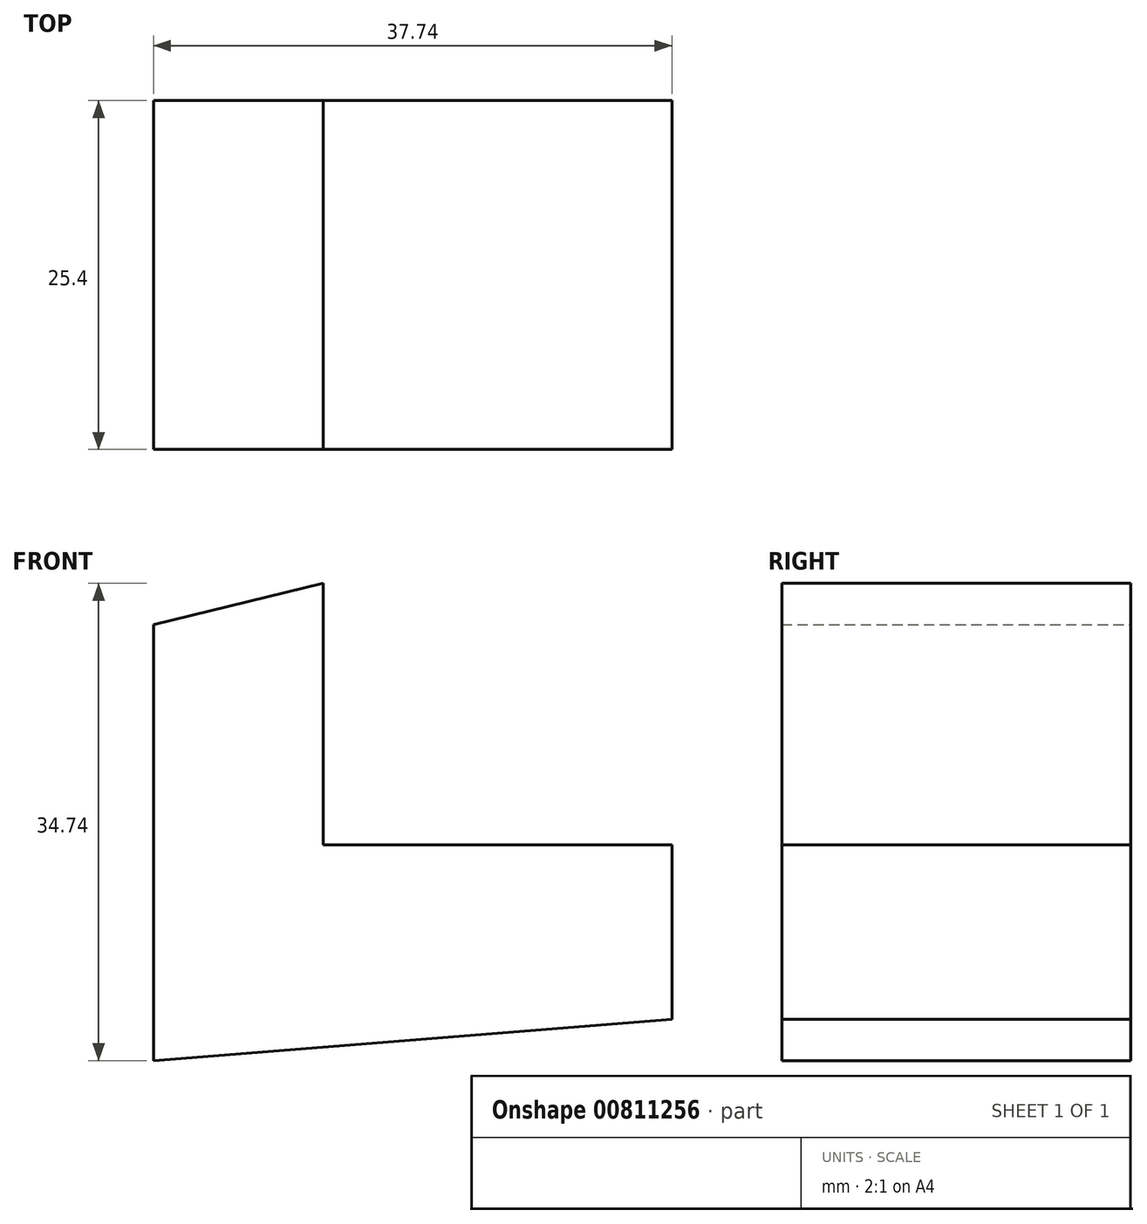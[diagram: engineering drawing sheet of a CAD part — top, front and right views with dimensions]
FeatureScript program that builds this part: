
annotation { "Feature Type Name" : "Feature", "Feature Type Description" : "" }
export const myFeature = defineFeature(function(context is Context, id is Id, definition is map)
    precondition{}
    {
        {
            var Q0;
            Q0=qCreatedBy(makeId("Front.planeOp"),FACE);
            var sketch = newSketch(context, id + "F0", { "sketchPlane" : qUnion([Q0])});
            skLineSegment(sketch, "E0", {"start": v(0, 0) * mm, "end": v(0, 31.75) * mm});
            skLineSegment(sketch, "E1", {"start": v(0, 31.75) * mm, "end": v(12.34, 34.74) * mm});
            skLineSegment(sketch, "E2", {"start": v(12.34, 34.74) * mm, "end": v(12.34, 15.7) * mm});
            skLineSegment(sketch, "E3", {"start": v(12.34, 15.7) * mm, "end": v(37.74, 15.7) * mm});
            skLineSegment(sketch, "E4", {"start": v(37.74, 15.7) * mm, "end": v(37.74, 3) * mm});
            skLineSegment(sketch, "E5", {"start": v(37.74, 3) * mm, "end": v(0, 0) * mm});
            skSolve(sketch);
        }
        {
            var Q0;
            Q0 = qSketchRegion(id + "F0", true);
            extrude(context, id + "F1", {"entities" : qUnion([Q0]), "depth" : 25.4 * mm, "offsetDistance" : 25.4 * mm});
        }
    });
